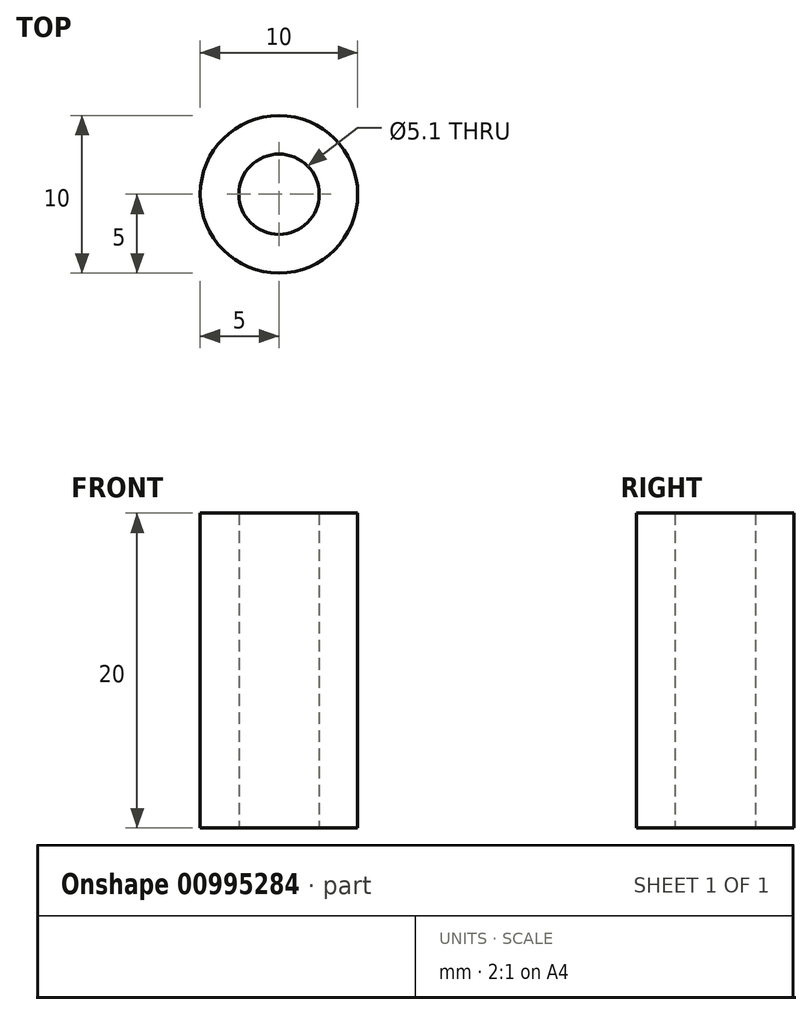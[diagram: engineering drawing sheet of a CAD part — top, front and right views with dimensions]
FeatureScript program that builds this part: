
annotation { "Feature Type Name" : "Feature", "Feature Type Description" : "" }
export const myFeature = defineFeature(function(context is Context, id is Id, definition is map)
    precondition{}
    {
        {
            var Q0;
            Q0=qCreatedBy(makeId("Top.planeOp"),FACE);
            var sketch = newSketch(context, id + "F0", { "sketchPlane" : qUnion([Q0])});
            skCircle(sketch, "E0", {"center": v(0, 0) * mm, "radius": 2.55 * mm});
            skCircle(sketch, "E1", {"center": v(0, 0) * mm, "radius": 5 * mm});
            skSolve(sketch);
        }
        {
            var Q0;
            Q0=makeQuery(id+"F0.imprint","IMPRINT",FACE,{"disambiguationData":[TD([[makeQuery(id+"F0.imprint","IMPRINT",EDGE,{"derivedFrom":sQuery(id+"F0.wireOp",EDGE,"E0")}),-1.0]])]});
            extrude(context, id + "F1", {"entities" : qUnion([Q0]), "depth" : 20 * mm, "offsetDistance" : 25 * mm});
        }
    });
